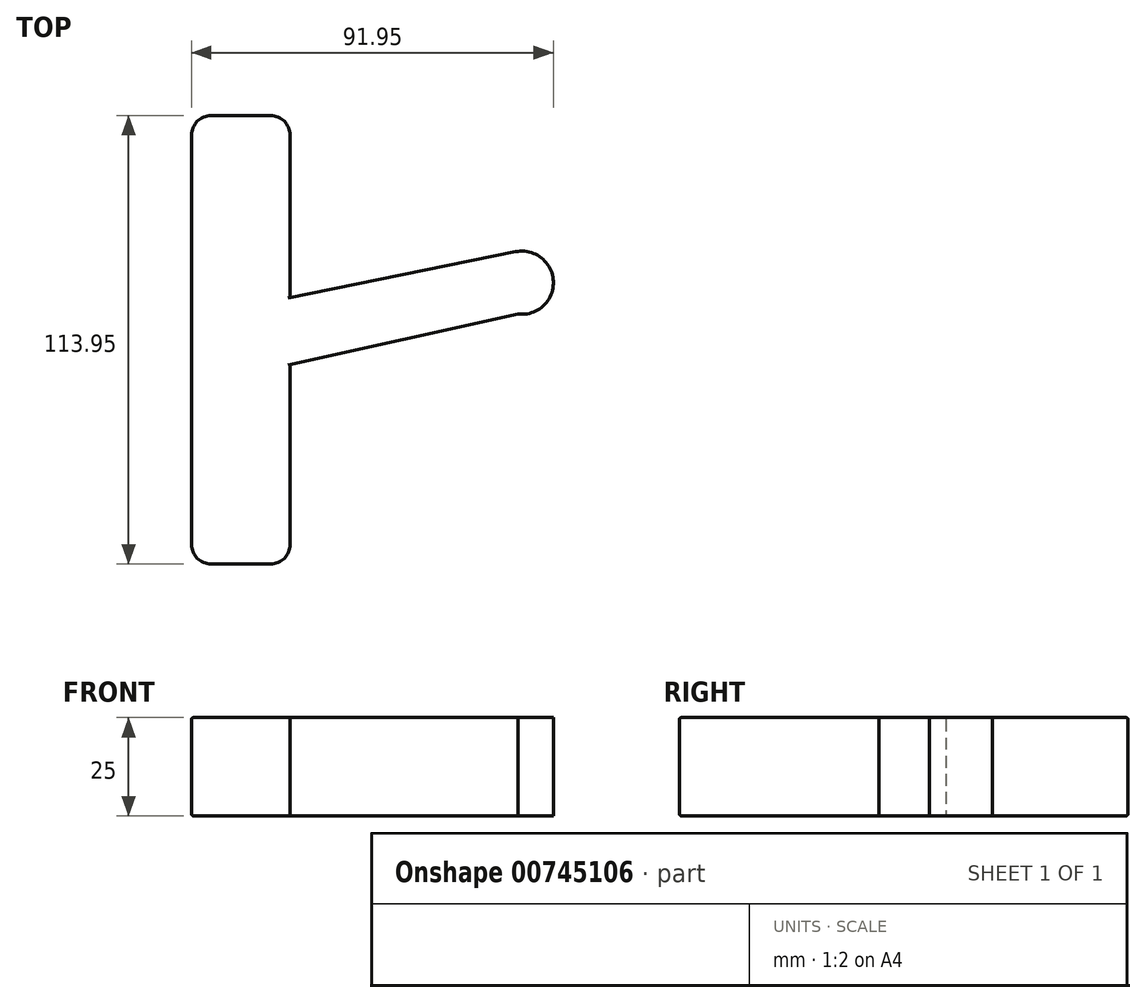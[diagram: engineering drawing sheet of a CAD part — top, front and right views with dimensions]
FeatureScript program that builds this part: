
annotation { "Feature Type Name" : "Feature", "Feature Type Description" : "" }
export const myFeature = defineFeature(function(context is Context, id is Id, definition is map)
    precondition{}
    {
        {
            var Q0;
            Q0=qCreatedBy(makeId("Top.planeOp"),FACE);
            var sketch = newSketch(context, id + "F0", { "sketchPlane" : qUnion([Q0])});
            skLineSegment(sketch, "E0", {"start": v(-50.04, 42.2) * mm, "end": v(-34.98, 42.2) * mm});
            skLineSegment(sketch, "E1", {"start": v(-29.98, 37.2) * mm, "end": v(-29.98, -66.74) * mm});
            skLineSegment(sketch, "E2", {"start": v(-34.98, -71.74) * mm, "end": v(-50.04, -71.74) * mm});
            skLineSegment(sketch, "E3", {"start": v(-55.04, -66.74) * mm, "end": v(-55.04, 37.2) * mm});
            skPoint(sketch, "E4.visualSharp", {"position": v(-29.98, 42.2) * mm});
            skArc(sketch, "E4.filletArc", {"start": v(-29.98, 37.2) * mm, "mid": v(-31.44, 40.74) * mm, "end": v(-34.98, 42.2) * mm});
            skPoint(sketch, "E5.visualSharp", {"position": v(-55.04, 42.2) * mm});
            skArc(sketch, "E5.filletArc", {"start": v(-50.04, 42.2) * mm, "mid": v(-53.57, 40.74) * mm, "end": v(-55.04, 37.2) * mm});
            skPoint(sketch, "E6.visualSharp", {"position": v(-55.04, -71.74) * mm});
            skArc(sketch, "E6.filletArc", {"start": v(-55.04, -66.74) * mm, "mid": v(-53.57, -70.28) * mm, "end": v(-50.04, -71.74) * mm});
            skPoint(sketch, "E7.visualSharp", {"position": v(-29.98, -71.74) * mm});
            skArc(sketch, "E7.filletArc", {"start": v(-34.98, -71.74) * mm, "mid": v(-31.44, -70.28) * mm, "end": v(-29.98, -66.74) * mm});
            skLineSegment(sketch, "E8", {"start": v(-29.98, -4.03) * mm, "end": v(27.3, 7.6) * mm});
            skArc(sketch, "E9", {"start": v(27.3, 7.6) * mm, "mid": v(36.9, 0.05) * mm, "end": v(27.9, -8.2) * mm});
            skLineSegment(sketch, "E10", {"start": v(27.9, -8.2) * mm, "end": v(-29.98, -21.03) * mm});
            skSolve(sketch);
        }
        {
            var Q0;
            {var subQ0=sQuery(id+"F0.wireOp",EDGE,"E8");Q0=makeQuery(id+"F0.imprint","IMPRINT",FACE,{"disambiguationData":[TD([[makeQuery(id+"F0.imprint","IMPRINT",EDGE,{"derivedFrom":subQ0}),-1.0]])]});}
            var Q1;
            Q1=makeQuery(id+"F0.imprint","IMPRINT",FACE,{"disambiguationData":[TD([[makeQuery(id+"F0.imprint","IMPRINT",EDGE,{"derivedFrom":sQuery(id+"F0.wireOp",EDGE,"E0")}),-1.0]])]});
            extrude(context, id + "F1", {"entities" : qUnion([Q0, Q1]), "depth" : 25 * mm, "offsetDistance" : 25 * mm});
        }
        {
            var Q0;
            Q0=makeQuery(id+"F1.opExtrude","SWEPT_FACE",FACE,{"disambiguationData":[OSD([sQuery(id+"F0.wireOp",EDGE,"E10")])]});
            var sketch = newSketch(context, id + "F2", { "sketchPlane" : qUnion([Q0])});
            skCircle(sketch, "E11", {"center": v(8.45, 12.5) * mm, "radius": 5.01 * mm});
            skPoint(sketch, "E11.centerSnap0", {"position": v(25.45, 12.5) * mm});
            skCircle(sketch, "E12", {"center": v(8.45, 12.5) * mm, "radius": 4.4 * mm});
            skCircle(sketch, "E13", {"center": v(8.45, 12.5) * mm, "radius": 5.7 * mm});
            skSolve(sketch);
        }
        {
            var Q0;
            Q0=sQuery(id+"F2.wireOp",EDGE,"E13");
            var Q1;
            Q1=sQuery(id+"F2.wireOp",EDGE,"E11");
            extrude(context, id + "F3", {"bodyType" : ToolBodyType.SURFACE, "surfaceEntities" : qUnion([Q0, Q1]), "depth" : 4 * mm, "offsetDistance" : 25 * mm});
        }
        {
            var Q0;
            {var subQ0=sQuery(id+"F0.wireOp",EDGE,"E1");Q0=makeQuery(id+"F1.opExtrude","CAP_EDGE",EDGE,{"disambiguationData":[OSD([subQ0]),TDD([makeQuery(id+"F0.imprint","IMPRINT",EDGE,{"disambiguationData":[TD([[makeQuery(id+"F0.imprint","INTERSECT",VERTEX,{"derivedFrom":[subQ0,sQuery(id+"F0.wireOp",EDGE,"E7.filletArc")]}),1.0]])],"derivedFrom":subQ0})])],"isStart":false});}
            fillet(context, id + "F4", {"entities" : qUnion([Q0]), "radius" : 0.53 * mm, "tangentPropagation" : true, "allowEdgeOverflow" : false});
        }
        {
            var Q0;
            {var subQ0=sQuery(id+"F0.wireOp",EDGE,"E1");Q0=makeQuery(id+"F1.opExtrude","CAP_EDGE",EDGE,{"disambiguationData":[OSD([subQ0]),TDD([makeQuery(id+"F0.imprint","IMPRINT",EDGE,{"disambiguationData":[TD([[makeQuery(id+"F0.imprint","INTERSECT",VERTEX,{"derivedFrom":[subQ0,sQuery(id+"F0.wireOp",EDGE,"E7.filletArc")]}),1.0]])],"derivedFrom":subQ0})])],"isStart":true});}
            fillet(context, id + "F5", {"entities" : qUnion([Q0]), "radius" : 0.5 * mm, "tangentPropagation" : true, "allowEdgeOverflow" : false});
        }
    });
